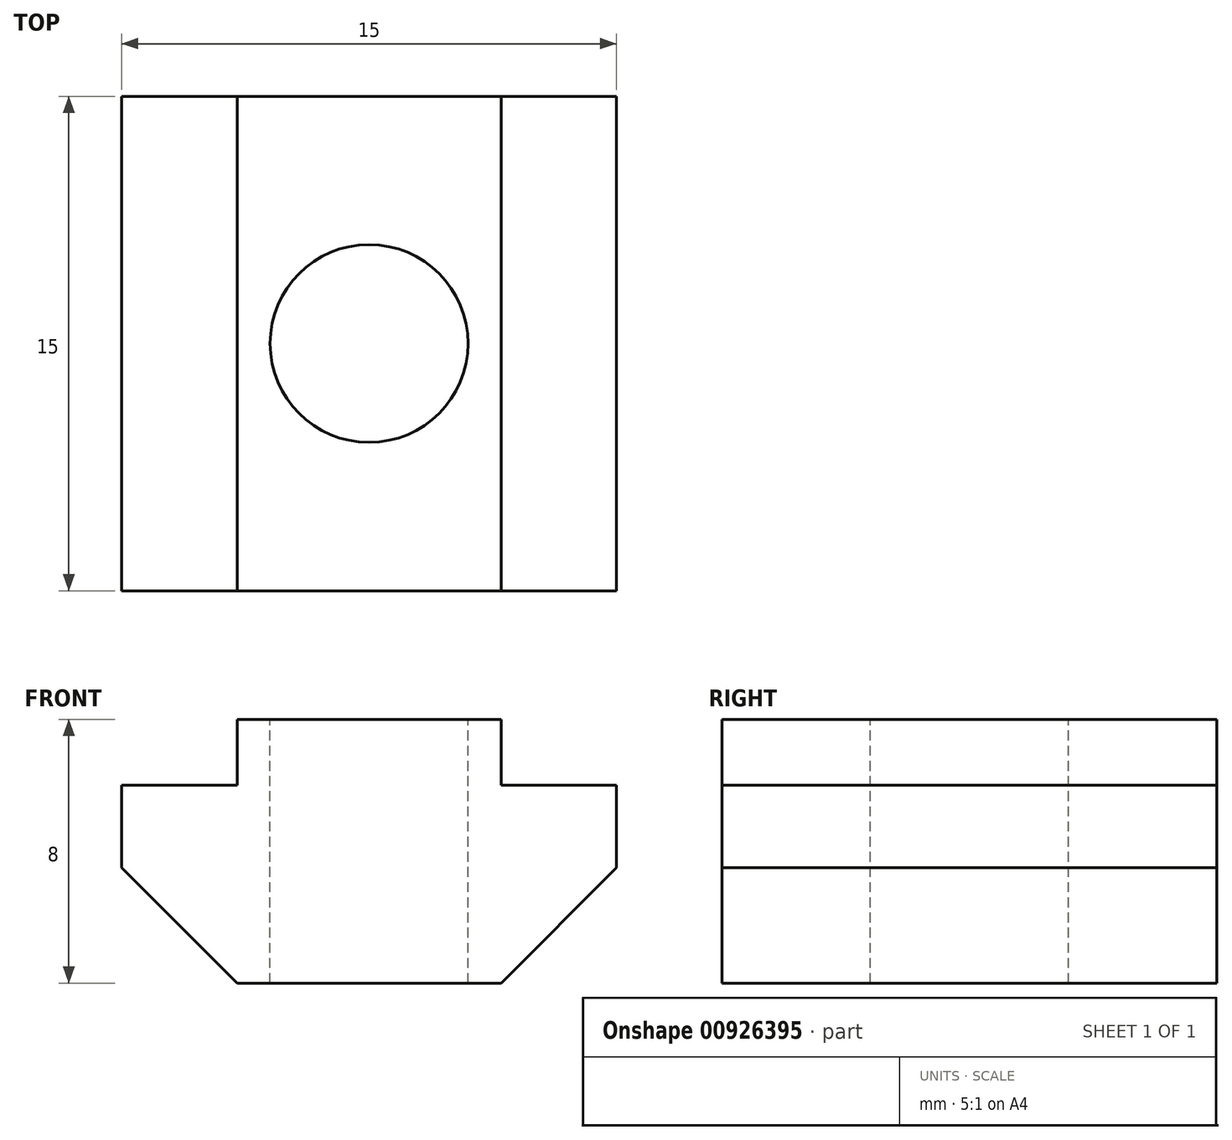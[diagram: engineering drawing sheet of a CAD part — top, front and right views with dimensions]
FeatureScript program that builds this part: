
annotation { "Feature Type Name" : "Feature", "Feature Type Description" : "" }
export const myFeature = defineFeature(function(context is Context, id is Id, definition is map)
    precondition{}
    {
        {
            var Q0;
            Q0=qCreatedBy(makeId("Front.planeOp"),FACE);
            var sketch = newSketch(context, id + "F0", { "sketchPlane" : qUnion([Q0])});
            skLineSegment(sketch, "E0", {"start": v(0, 0) * mm, "end": v(4, 0) * mm});
            skLineSegment(sketch, "E1", {"start": v(4, 0) * mm, "end": v(7.5, 3.5) * mm});
            skLineSegment(sketch, "E2", {"start": v(7.5, 3.5) * mm, "end": v(7.5, 6) * mm});
            skLineSegment(sketch, "E3", {"start": v(7.5, 6) * mm, "end": v(4, 6) * mm});
            skLineSegment(sketch, "E4", {"start": v(4, 6) * mm, "end": v(4, 8) * mm});
            skLineSegment(sketch, "E5", {"start": v(4, 8) * mm, "end": v(0, 8) * mm});
            skLineSegment(sketch, "E6", {"start": v(0, 8) * mm, "end": v(0, 0) * mm, "construction": true});
            skLineSegment(sketch, "E7.MirrorCS", {"start": v(-4, 0) * mm, "end": v(-7.5, 3.5) * mm});
            skLineSegment(sketch, "E8.MirrorCS", {"start": v(-7.5, 3.5) * mm, "end": v(-7.5, 6) * mm});
            skLineSegment(sketch, "E9.MirrorCS", {"start": v(-7.5, 6) * mm, "end": v(-4, 6) * mm});
            skLineSegment(sketch, "E10.MirrorCS", {"start": v(-4, 8) * mm, "end": v(0, 8) * mm});
            skLineSegment(sketch, "E11.MirrorCS", {"start": v(-4, 6) * mm, "end": v(-4, 8) * mm});
            skLineSegment(sketch, "E12.MirrorCS", {"start": v(0, 0) * mm, "end": v(-4, 0) * mm});
            skSolve(sketch);
        }
        {
            var Q0;
            Q0=qSketchRegion(id+"F0",true);
            extrude(context, id + "F1", {"entities" : qUnion([Q0]), "depth" : 15 * mm, "offsetDistance" : 25 * mm});
        }
        {
            var Q0;
            Q0=makeQuery(id+"F1.opExtrude","SWEPT_FACE",FACE,{"disambiguationData":[OSD([sQuery(id+"F0.wireOp",EDGE,"E5"),sQuery(id+"F0.wireOp",EDGE,"E10.MirrorCS")])]});
            var sketch = newSketch(context, id + "F2", { "sketchPlane" : qUnion([Q0])});
            skLineSegment(sketch, "E13", {"start": v(0, -15) * mm, "end": v(0, 0) * mm, "construction": true});
            skLineSegment(sketch, "E14", {"start": v(-4, -7.5) * mm, "end": v(4, -7.5) * mm, "construction": true});
            skCircle(sketch, "E15", {"center": v(0, -7.5) * mm, "radius": 3 * mm});
            skSolve(sketch);
        }
        {
            var Q0;
            Q0=qSketchRegion(id+"F2",true);
            extrude(context, id + "F3", {"entities" : qUnion([Q0]), "operationType" : NewBodyOperationType.REMOVE, "endBound" : BoundingType.THROUGH_ALL, "oppositeDirection" : true, "depth" : 25 * mm, "offsetDistance" : 25 * mm});
        }
    });
